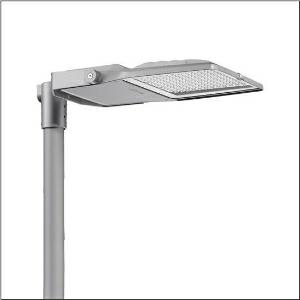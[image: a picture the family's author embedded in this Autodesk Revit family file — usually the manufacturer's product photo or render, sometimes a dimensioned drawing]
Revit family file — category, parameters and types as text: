
# Revit family: floodlight_fl_21_iq_midi___pl52_5xa7781f4d3a_7000
name_source: partatom
category: Lighting Fixtures
units: mm (PartAtom-declared; Revit-internal decimal feet)

## family parameters
Cut with Voids When Loaded = No
Host = Face
Light Source = No
Part Type = Normal
Room Calculation Point = No
Round Connector Dimension = Use Diameter
Shared = No

## types (1)
- --- (1 x LED, 37330 lm, 270.2 W, 4000K)
    Apparent Load = 270 VA
    CIE Flux Codes = 26 60 98 100 100
    Color Rendering = 70
    Color Temperature = 4000K
    Default Elevation = 1800 mm
    Description = Floodlight FL 21 iQ midi, floodlight, primary light control with lens, of PMMA, primary optical cover: protective disc, of toughened safety glass, transparent, light distribution: PL52, light emission: direct distribution, installation type: surface-mounted, LED, High Power LED, rated luminous flux: 37.330lm, luminous efficacy: 138lm/W, light colour: 740, colour temperature: 4000K, control gear: iQ Comfort/DALI, control: optimised constant luminous flux control (CLO 2.0), Desk-Remote (wireless, voltage-free reading and setting of iQ features in the workshop via application-optimized NFC function/RFID function), Light-Fading, Smart-Wire, Night-Set, Lumen-Switch, Temp-Guard, Auto-Match, with terminal, 6-pole, mains connection: 220..240V, AC, 50/60Hz, start of lifetime: 270W, end of service life: 287W, reduction: 118W, luminaire housing, of diecast aluminium, powder-coated, Siteco® metallic grey (DB 702S), corrosivity category C5 mid according to DIN EN ISO 12944, suitable for swimming pools, chlorine-resistant, sealing non-destructively replaceable, please order mast flange separately, mast bracket, of steel, galvanised, powder-coated, Siteco® metallic grey (DB 702S), protection rating (complete): IP66, insulation class (complete): insulation class II (safety insulation), certification: CE, ENEC, VDE, protection symbol: D, impact resistance: IK08, permissible operating ambient temperature: -40..+40°C, permissible operating ambient temperature for outdoor applications: -40..+50°C, standard: DIN EN 12944, LABS conformity tested according to VDMA 24364:2018-05, packaging unit: 1 piece

Light Distribution: PL52
    Height = 76 mm
    Lamp = 1 x LED
    Lamp Light Flux = 37330 lm
    Lamp Power = 270.2 W
    Lamp count = 1
    Length = 657 mm
    Luminous efficacy = 138 lm/W
    Manufacturer = Siteco
    ModVariant = No
    Model = 5XA7781F4D3A
    Number of Poles = 1
    OnlyDefault = Yes
    Power Factor = 1
    Product Name = Floodlight FL 21 iQ midi | PL52
    Product group = floodlight | pylon annexe
    ProductGroupID = 6201
    Protection Class = Protection class II
    Protection Degree = IP 66
    RLX_Detail_Level = 1
    RLX_Emergency_Light_Flux = 0 lm
    RLX_Emergency_Type = 0
    RLX_Emergency_Type_DB = No
    RlxData = <blob elided: 154069 chars, md5=98f4cb62>
    Socket = socket
    Standby Power = 0 W
    System Light Flux = 37330 lm
    System Power = 270 W
    Type Comments = factory setting: luminous flux: 100 % | dim-lin: 254 | 620 mA
    Type Image = l_1007123.jpg
    URL = http://relux.com
    VarID = @adj_127183
    Voltage = 0 V
    Weight = 0.00 kg
    Width = 442 mm

## geometry (parser evidence)
native form markers: Blend x4, Sweep x15
no freeform markers — native parametric forms only
